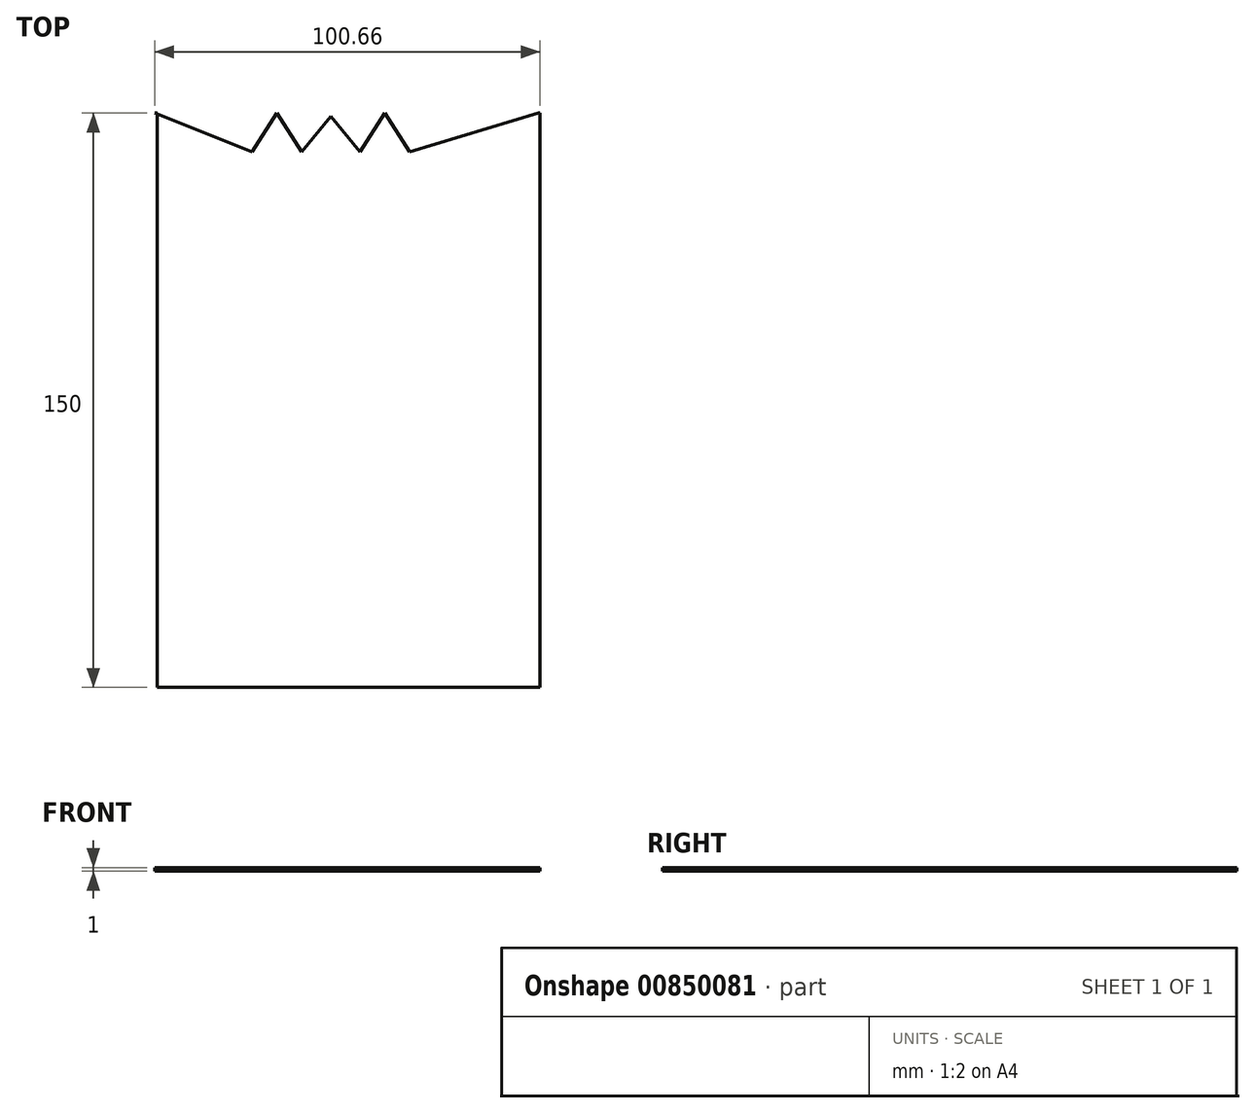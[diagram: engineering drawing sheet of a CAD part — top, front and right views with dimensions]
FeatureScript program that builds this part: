
annotation { "Feature Type Name" : "Feature", "Feature Type Description" : "" }
export const myFeature = defineFeature(function(context is Context, id is Id, definition is map)
    precondition{}
    {
        {
            var Q0;
            Q0=qCreatedBy(makeId("Top.planeOp"),FACE);
            var sketch = newSketch(context, id + "F0", { "sketchPlane" : qUnion([Q0])});
            skLineSegment(sketch, "E0", {"start": v(-53, 66.75) * mm, "end": v(-53, -83.25) * mm});
            skLineSegment(sketch, "E1", {"start": v(-53, -83.25) * mm, "end": v(47, -83.25) * mm});
            skLineSegment(sketch, "E2", {"start": v(47, -83.25) * mm, "end": v(47, 66.75) * mm});
            skLineSegment(sketch, "E3", {"start": v(47, 66.75) * mm, "end": v(46.63, 66.75) * mm});
            skPoint(sketch, "E4.endSnap0", {"position": v(-3, 66.75) * mm});
            skPoint(sketch, "E4.end.orphan", {"position": v(0, 66.75) * mm});
            skLineSegment(sketch, "E5", {"start": v(-53.66, 66.75) * mm, "end": v(-28.2, 56.64) * mm});
            skLineSegment(sketch, "E6", {"start": v(-28.2, 56.64) * mm, "end": v(-21.75, 66.75) * mm});
            skLineSegment(sketch, "E7", {"start": v(-21.75, 66.75) * mm, "end": v(-15.3, 56.64) * mm});
            skLineSegment(sketch, "E8", {"start": v(-15.3, 56.64) * mm, "end": v(-7.65, 65.88) * mm});
            skLineSegment(sketch, "E9", {"start": v(-7.65, 65.88) * mm, "end": v(0, 56.64) * mm});
            skLineSegment(sketch, "E10", {"start": v(0, 56.64) * mm, "end": v(6.45, 66.75) * mm});
            skLineSegment(sketch, "E11", {"start": v(6.45, 66.75) * mm, "end": v(12.9, 56.64) * mm});
            skLineSegment(sketch, "E12", {"start": v(12.9, 56.64) * mm, "end": v(46.63, 66.75) * mm});
            skLineSegment(sketch, "E13.trimOffspring", {"start": v(-53, 66.75) * mm, "end": v(-53.66, 66.75) * mm});
            skSolve(sketch);
        }
        {
            var Q0;
            Q0 = qSketchRegion(id + "F0", true);
            extrude(context, id + "F1", {"entities" : qUnion([Q0]), "depth" : 1 * mm, "offsetDistance" : 25 * mm});
        }
    });
